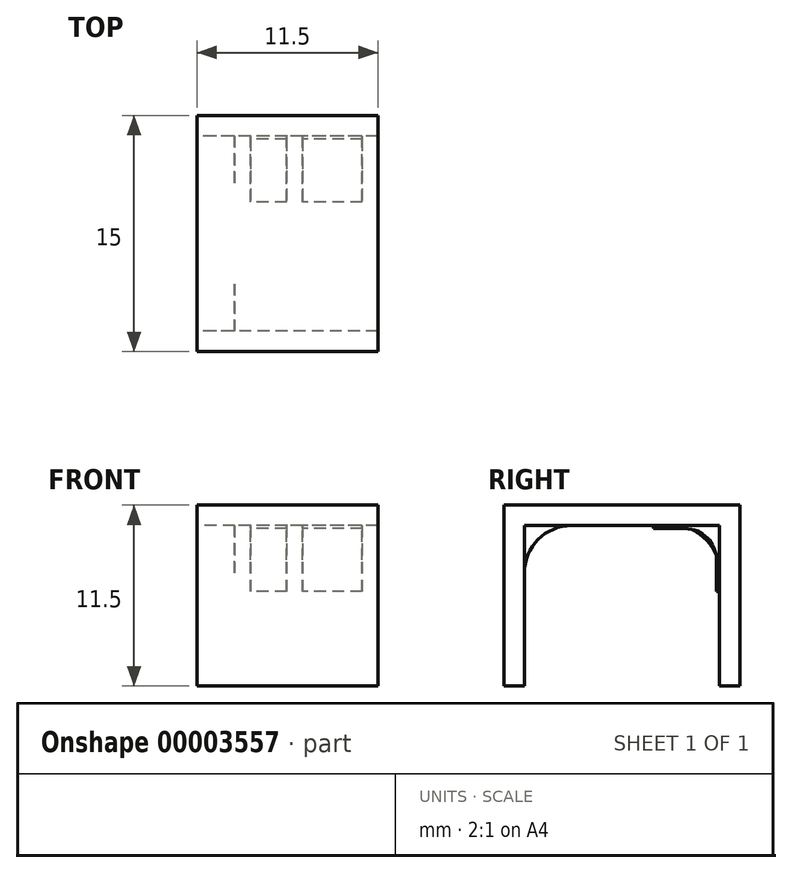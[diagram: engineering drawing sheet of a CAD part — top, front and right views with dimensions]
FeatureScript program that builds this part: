
annotation { "Feature Type Name" : "Feature", "Feature Type Description" : "" }
export const myFeature = defineFeature(function(context is Context, id is Id, definition is map)
    precondition{}
    {
        {
            var Q0;
            Q0=qCreatedBy(makeId("Top.planeOp"),FACE);
            var sketch = newSketch(context, id + "F0", { "sketchPlane" : qUnion([Q0])});
            skLineSegment(sketch, "E0.bottom", {"start": v(0, 0) * mm, "end": v(11.5, 0) * mm});
            skLineSegment(sketch, "E0.top", {"start": v(0, 15) * mm, "end": v(11.5, 15) * mm});
            skLineSegment(sketch, "E0.left", {"start": v(0, 0) * mm, "end": v(0, 15) * mm});
            skLineSegment(sketch, "E0.right", {"start": v(11.5, 0) * mm, "end": v(11.5, 15) * mm});
            skSolve(sketch);
        }
        {
            var Q0;
            Q0 = qSketchRegion(id + "F0", true);
            extrude(context, id + "F1", {"entities" : qUnion([Q0]), "depth" : 11.5 * mm});
        }
        {
            var Q0;
            Q0=makeQuery(id+"F1.opExtrude","SWEPT_FACE",FACE,{"disambiguationData":[OSD([sQuery(id+"F0.wireOp",EDGE,"E0.left")])]});
            var sketch = newSketch(context, id + "F2", { "sketchPlane" : qUnion([Q0])});
            skLineSegment(sketch, "E1.bottom", {"start": v(-13.7, 0) * mm, "end": v(-1.3, 0) * mm});
            skLineSegment(sketch, "E1.top", {"start": v(-13.7, 10.2) * mm, "end": v(-1.3, 10.2) * mm});
            skLineSegment(sketch, "E1.left", {"start": v(-13.7, 0) * mm, "end": v(-13.7, 10.2) * mm});
            skLineSegment(sketch, "E1.right", {"start": v(-1.3, 0) * mm, "end": v(-1.3, 10.2) * mm});
            skLineSegment(sketch, "E2", {"start": v(-13.7, 5.1) * mm, "end": v(-15, 5.1) * mm, "construction": true});
            skLineSegment(sketch, "E3", {"start": v(-1.3, 5.1) * mm, "end": v(0, 5.1) * mm, "construction": true});
            skSolve(sketch);
        }
        {
            var Q0;
            Q0 = qSketchRegion(id + "F2", true);
            extrude(context, id + "F3", {"entities" : qUnion([Q0]), "operationType" : NewBodyOperationType.REMOVE, "endBound" : BoundingType.THROUGH_ALL, "oppositeDirection" : true, "depth" : 25 * mm});
        }
        {
            var Q0;
            Q0=makeQuery(id+"F1.opExtrude","SWEPT_FACE",FACE,{"disambiguationData":[OSD([sQuery(id+"F0.wireOp",EDGE,"E0.left")])]});
            var sketch = newSketch(context, id + "F4", { "sketchPlane" : qUnion([Q0])});
            skLineSegment(sketch, "E4", {"start": v(-7.5, 10.2) * mm, "end": v(-7.5, 0) * mm, "construction": true});
            skPoint(sketch, "E5.visualSharp", {"position": v(-13.7, 10.2) * mm});
            skArc(sketch, "E5.filletArc", {"start": v(-10.7, 10.2) * mm, "mid": v(-12.82, 9.32) * mm, "end": v(-13.7, 7.2) * mm});
            skLineSegment(sketch, "E6", {"start": v(-13.7, 7.2) * mm, "end": v(-13.7, 10.2) * mm});
            skLineSegment(sketch, "E7", {"start": v(-10.7, 10.2) * mm, "end": v(-13.7, 10.2) * mm});
            skArc(sketch, "E8.0.MirrorCS", {"start": v(-4.3, 10.2) * mm, "mid": v(-2.18, 9.32) * mm, "end": v(-1.3, 7.2) * mm});
            skLineSegment(sketch, "E9.0.MirrorCS", {"start": v(-4.3, 10.2) * mm, "end": v(-1.3, 10.2) * mm});
            skLineSegment(sketch, "E10.0.MirrorCS", {"start": v(-1.3, 7.2) * mm, "end": v(-1.3, 10.2) * mm});
            skSolve(sketch);
        }
        {
            var Q0;
            Q0 = qSketchRegion(id + "F4", true);
            extrude(context, id + "F5", {"entities" : qUnion([Q0]), "operationType" : NewBodyOperationType.ADD, "oppositeDirection" : true, "depth" : 2.5 * mm});
        }
        {
            var Q0;
            Q0=makeQuery(id+"F5.opExtrude","CAP_FACE",FACE,{"disambiguationData":[OSD([sQuery(id+"F4.wireOp",EDGE,"E5.filletArc"),sQuery(id+"F4.wireOp",EDGE,"E6"),sQuery(id+"F4.wireOp",EDGE,"E7")])],"isStart":false});
            cPlane(context, id + "F6", {"entities" : qUnion([Q0]), "cplaneType" : CPlaneType.OFFSET, "offset" : 0.8 * mm, "width" : 150 * mm, "height" : 150 * mm});
        }
        {
            var Q0;
            Q0=qCreatedBy(id+"F6.planeOp",FACE);
            var sketch = newSketch(context, id + "F7", { "sketchPlane" : qUnion([Q0])});
            skLineSegment(sketch, "E11", {"start": v(13.7, 6) * mm, "end": v(13.5, 6) * mm});
            skLineSegment(sketch, "E12", {"start": v(13.5, 6) * mm, "end": v(13.5, 8) * mm});
            skLineSegment(sketch, "E13", {"start": v(11.5, 10) * mm, "end": v(9.5, 10) * mm});
            skLineSegment(sketch, "E14", {"start": v(9.5, 10) * mm, "end": v(9.5, 10.2) * mm});
            skLineSegment(sketch, "E15", {"start": v(9.5, 10.2) * mm, "end": v(13.7, 10.2) * mm});
            skLineSegment(sketch, "E16", {"start": v(13.7, 10.2) * mm, "end": v(13.7, 6) * mm});
            skPoint(sketch, "E17.visualSharp", {"position": v(13.5, 10) * mm});
            skArc(sketch, "E17.filletArc", {"start": v(13.5, 8) * mm, "mid": v(12.91, 9.41) * mm, "end": v(11.5, 10) * mm});
            skSolve(sketch);
        }
        {
            var Q0;
            Q0 = qSketchRegion(id + "F7", true);
            extrude(context, id + "F8", {"entities" : qUnion([Q0]), "operationType" : NewBodyOperationType.ADD, "depth" : 2.5 * mm});
        }
        {
            var Q0;
            Q0=makeQuery(id+"F8.opExtrude","CAP_FACE",FACE,{"disambiguationData":[OSD([sQuery(id+"F7.wireOp",EDGE,"E11"),sQuery(id+"F7.wireOp",EDGE,"E12"),sQuery(id+"F7.wireOp",EDGE,"E13"),sQuery(id+"F7.wireOp",EDGE,"E14"),sQuery(id+"F7.wireOp",EDGE,"E15"),sQuery(id+"F7.wireOp",EDGE,"E16"),sQuery(id+"F7.wireOp",EDGE,"E17.filletArc")])],"isStart":false});
            cPlane(context, id + "F9", {"entities" : qUnion([Q0]), "cplaneType" : CPlaneType.OFFSET, "offset" : 0.8 * mm, "width" : 150 * mm, "height" : 150 * mm});
        }
        {
            var Q0;
            Q0=qCreatedBy(id+"F9.planeOp",FACE);
            var sketch = newSketch(context, id + "F10", { "sketchPlane" : qUnion([Q0])});
            skLineSegment(sketch, "E18.0.0", {"start": v(13.7, 6) * mm, "end": v(13.5, 6) * mm});
            skLineSegment(sketch, "E18.0.1", {"start": v(13.7, 10.2) * mm, "end": v(13.7, 6) * mm});
            skLineSegment(sketch, "E18.0.2", {"start": v(9.5, 10.2) * mm, "end": v(13.7, 10.2) * mm});
            skLineSegment(sketch, "E18.0.3", {"start": v(9.5, 10) * mm, "end": v(9.5, 10.2) * mm});
            skLineSegment(sketch, "E18.0.4", {"start": v(11.5, 10) * mm, "end": v(9.5, 10) * mm});
            skArc(sketch, "E18.0.5", {"start": v(13.5, 8) * mm, "mid": v(12.91, 9.41) * mm, "end": v(11.5, 10) * mm});
            skLineSegment(sketch, "E18.0.6", {"start": v(13.5, 6) * mm, "end": v(13.5, 8) * mm});
            skSolve(sketch);
        }
        {
            var Q0;
            Q0 = qSketchRegion(id + "F10", true);
            extrude(context, id + "F11", {"entities" : qUnion([Q0]), "operationType" : NewBodyOperationType.ADD, "depth" : 4 * mm});
        }
        {
            var Q0;
            {var subQ0=sQuery(id+"F0.wireOp",EDGE,"E0.bottom");var subQ1=sQuery(id+"F0.wireOp",EDGE,"E0.left");var subQ2=sQuery(id+"F0.wireOp",EDGE,"E0.right");Q0=makeQuery(id+"F3.boolean.opBoolean","SPLIT",FACE,{"disambiguationData":[TD([makeQuery(id+"F1.opExtrude","SWEPT_FACE",FACE,{"disambiguationData":[OSD([subQ0])]})])],"derivedFrom":makeQuery(id+"F1.opExtrude","CAP_FACE",FACE,{"disambiguationData":[OSD([subQ0,sQuery(id+"F0.wireOp",EDGE,"E0.top"),subQ1,subQ2])],"isStart":true})});}
            var sketch = newSketch(context, id + "F12", { "sketchPlane" : qUnion([Q0])});
            skLineSegment(sketch, "E19.bottom", {"start": v(10.6, -13.7) * mm, "end": v(10.5, -13.7) * mm});
            skLineSegment(sketch, "E19.top", {"start": v(10.6, -1.3) * mm, "end": v(10.5, -1.3) * mm});
            skLineSegment(sketch, "E19.left", {"start": v(10.6, -13.7) * mm, "end": v(10.6, -1.3) * mm});
            skLineSegment(sketch, "E19.right", {"start": v(10.5, -13.7) * mm, "end": v(10.5, -1.3) * mm});
            skLineSegment(sketch, "E20.bottom", {"start": v(6.7, -13.7) * mm, "end": v(6.6, -13.7) * mm});
            skLineSegment(sketch, "E20.top", {"start": v(6.7, -1.3) * mm, "end": v(6.6, -1.3) * mm});
            skLineSegment(sketch, "E20.left", {"start": v(6.7, -13.7) * mm, "end": v(6.7, -1.3) * mm});
            skLineSegment(sketch, "E20.right", {"start": v(6.6, -13.7) * mm, "end": v(6.6, -1.3) * mm});
            skLineSegment(sketch, "E21.bottom", {"start": v(5.8, -13.7) * mm, "end": v(5.7, -13.7) * mm});
            skLineSegment(sketch, "E21.top", {"start": v(5.8, -1.3) * mm, "end": v(5.7, -1.3) * mm});
            skLineSegment(sketch, "E21.left", {"start": v(5.8, -13.7) * mm, "end": v(5.8, -1.3) * mm});
            skLineSegment(sketch, "E21.right", {"start": v(5.7, -13.7) * mm, "end": v(5.7, -1.3) * mm});
            skLineSegment(sketch, "E22.bottom", {"start": v(3.4, -13.7) * mm, "end": v(3.3, -13.7) * mm});
            skLineSegment(sketch, "E22.top", {"start": v(3.4, -1.3) * mm, "end": v(3.3, -1.3) * mm});
            skLineSegment(sketch, "E22.left", {"start": v(3.4, -13.7) * mm, "end": v(3.4, -1.3) * mm});
            skLineSegment(sketch, "E22.right", {"start": v(3.3, -13.7) * mm, "end": v(3.3, -1.3) * mm});
            skLineSegment(sketch, "E23.bottom", {"start": v(2.5, -13.7) * mm, "end": v(2.4, -13.7) * mm});
            skLineSegment(sketch, "E23.top", {"start": v(2.5, -1.3) * mm, "end": v(2.4, -1.3) * mm});
            skLineSegment(sketch, "E23.left", {"start": v(2.5, -13.7) * mm, "end": v(2.5, -1.3) * mm});
            skLineSegment(sketch, "E23.right", {"start": v(2.4, -13.7) * mm, "end": v(2.4, -1.3) * mm});
            skSolve(sketch);
        }
        {
            var Q0;
            Q0 = qSketchRegion(id + "F12", true);
            var Q1;
            Q1=makeQuery(id+"F3.boolean.opBoolean","COPY",FACE,{"derivedFrom":makeQuery(id+"F3.opExtrude","SWEPT_FACE",FACE,{"disambiguationData":[OSD([sQuery(id+"F2.wireOp",EDGE,"E1.top")])]})});
            extrude(context, id + "F13", {"entities" : qUnion([Q0]), "operationType" : NewBodyOperationType.REMOVE, "endBound" : BoundingType.UP_TO_SURFACE, "oppositeDirection" : true, "endBoundEntityFace" : qUnion([Q1]), "depth" : 25 * mm});
        }
    });
